# Revit family: МПА_В_Е_1000_4000_А31_Eng
name_source: partatom
category: Mechanical Equipment
units: mm (PartAtom-declared; Revit-internal decimal feet)

## family parameters
Always vertical = Yes
Classification = None
Cut with Voids When Loaded = No
Part Type = Normal
Room Calculation Point = No
Round Connector Dimension = Use Diameter
Shared = No
Work Plane-Based = No

## types (40) — shared parameters
00_20_Manufacturer = Vents
00_20_Name = Air supply unit
BW2 = 80 mm  [stored 0.262467 ft]
Casing Material = Steel, galvanized
Filter = Coarse 90%/G4
Frequency = 50 Hz
L5 = 400 mm  [stored 1.31234 ft]
Load Classification = HVAC
Maintenance zone material = <By Category>
Manufacturer = Vents
URL = https://ventilation-system.com
zero-valued in all types: Default Elevation

## per-type parameters (varying)
- MPA 1000 W ЕС L А31: 00_20_Type=MPA 1000 W ЕС L А31; Amperage=1 A; B=746 mm; B1=653 mm; B2=600 mm; B3=706 mm; B31=400 mm  [stored 1.31234 ft]; BE=753 mm; BW1=720 mm; E=400 mm  [stored 1.31234 ft]; H=393 mm  [stored 1.28937 ft]; H1=373 mm  [stored 1.22375 ft]; H3=200 mm  [stored 0.656168 ft]; HE=293 mm; HW1=62 mm; HW2=312 mm; Height=393 mm  [stored 1.28937 ft]; L=840 mm; L1=770 mm; L3=250 mm  [stored 0.82021 ft]; L6=100 mm  [stored 0.328084 ft]; LN=620 mm; Left=Yes; Length=900 mm; Maximum Air Flow=920.0 m³/h; Number of Fase=1; Panel side=Yes; Power=165 W; Right=No; Voltage=230 V; Water=Yes; Width=746 mm; d=25 mm  [stored 0.082021 ft]; l1=385 mm  [stored 1.26312 ft]
- MPA 4000 W ЕС L А31: 00_20_Type=MPA 4000 W ЕС L А31; Amperage=1 A; B=1087 mm; B1=993 mm; B2=940 mm; B3=1046 mm; B31=700 mm; BE=1093 mm; BW1=1060 mm; E=570 mm; H=563 mm; H1=543 mm  [stored 1.7815 ft]; H3=400 mm  [stored 1.31234 ft]; HE=463 mm  [stored 1.51903 ft]; HW1=82 mm; HW2=462 mm; Height=563 mm; L=1140 mm; L1=1070 mm; L3=380 mm  [stored 1.24672 ft]; L6=100 mm  [stored 0.328084 ft]; LN=770 mm; Left=Yes; Length=1200 mm; Maximum Air Flow=4950.0 m³/h; Number of Fase=1; Panel side=Yes; Power=698 W; Right=No; Voltage=230 V; Water=Yes; Width=1087 mm; d=35 mm  [stored 0.114829 ft]; l1=535 mm  [stored 1.75525 ft]
- MPA 1000 Е-6.0 ЕС L А31: 00_20_Type=MPA 1000 Е-6.0 ЕС L А31; Amperage=11 A; B=746 mm; B1=653 mm; B2=600 mm; B3=706 mm; B31=400 mm  [stored 1.31234 ft]; BE=753 mm; BW1=720 mm; E=400 mm  [stored 1.31234 ft]; H=393 mm  [stored 1.28937 ft]; H1=373 mm  [stored 1.22375 ft]; H3=200 mm  [stored 0.656168 ft]; HE=293 mm; HW1=62 mm; HW2=312 mm; Height=393 mm  [stored 1.28937 ft]; L=840 mm; L1=770 mm; L3=250 mm  [stored 0.82021 ft]; L6=220 mm  [stored 0.721785 ft]; LN=100 mm  [stored 0.328084 ft]; Left=Yes; Length=900 mm; Maximum Air Flow=1000.0 m³/h; Number of Fase=3; Panel side=Yes; Power=6165 W; Right=No; Voltage=400 V; Water=No; Width=746 mm; d=25 mm  [stored 0.082021 ft]; l1=385 mm  [stored 1.26312 ft]
- MPA 1500 W ЕС L А31: 00_20_Type=MPA 1500 W ЕС L А31; Amperage=2 A; B=847 mm; B1=754 mm; B2=700 mm; B3=808 mm; B31=500 mm  [stored 1.64042 ft]; BE=854 mm; BW1=820 mm; E=450 mm  [stored 1.47638 ft]; H=453 mm  [stored 1.48622 ft]; H1=433 mm; H3=250 mm  [stored 0.82021 ft]; HE=353 mm  [stored 1.15814 ft]; HW1=58 mm  [stored 0.190289 ft]; HW2=376 mm; Height=453 mm  [stored 1.48622 ft]; L=840 mm; L1=770 mm; L3=318 mm  [stored 1.04331 ft]; L6=100 mm  [stored 0.328084 ft]; LN=620 mm; Left=Yes; Length=900 mm; Maximum Air Flow=1145.0 m³/h; Number of Fase=1; Panel side=Yes; Power=222 W; Right=No; Voltage=230 V; Water=Yes; Width=847 mm; d=25 mm  [stored 0.082021 ft]; l1=385 mm  [stored 1.26312 ft]
- MPA 2000 W ЕС L А31: 00_20_Type=MPA 2000 W ЕС L А31; Amperage=2 A; B=847 mm; B1=754 mm; B2=700 mm; B3=808 mm; B31=500 mm  [stored 1.64042 ft]; BE=854 mm; BW1=820 mm; E=450 mm  [stored 1.47638 ft]; H=453 mm  [stored 1.48622 ft]; H1=433 mm; H3=300 mm; HE=353 mm  [stored 1.15814 ft]; HW1=58 mm  [stored 0.190289 ft]; HW2=376 mm; Height=453 mm  [stored 1.48622 ft]; L=840 mm; L1=770 mm; L3=318 mm  [stored 1.04331 ft]; L6=100 mm  [stored 0.328084 ft]; LN=620 mm; Left=Yes; Length=900 mm; Maximum Air Flow=2150.0 m³/h; Number of Fase=1; Panel side=Yes; Power=387 W; Right=No; Voltage=230 V; Water=Yes; Width=847 mm; d=25 mm  [stored 0.082021 ft]; l1=385 mm  [stored 1.26312 ft]
- MPA 3000 W ЕС L А31: 00_20_Type=MPA 3000 W ЕС L А31; Amperage=2 A; B=944 mm; B1=853 mm; B2=800 mm; B3=906 mm; B31=600 mm; BE=953 mm; BW1=920 mm; E=500 mm  [stored 1.64042 ft]; H=513 mm  [stored 1.68307 ft]; H1=493 mm  [stored 1.61745 ft]; H3=300 mm; HE=413 mm  [stored 1.35499 ft]; HW1=63 mm; HW2=431 mm; Height=513 mm  [stored 1.68307 ft]; L=1140 mm; L1=1070 mm; L3=368 mm  [stored 1.20735 ft]; L6=100 mm  [stored 0.328084 ft]; LN=770 mm; Left=Yes; Length=1200 mm; Maximum Air Flow=2930.0 m³/h; Number of Fase=1; Panel side=Yes; Power=425 W; Right=No; Voltage=230 V; Water=Yes; Width=944 mm; d=28 mm  [stored 0.0918635 ft]; l1=535 mm  [stored 1.75525 ft]
- MPA 1000 Е-12.0 ЕС L А31: 00_20_Type=MPA 1000 Е-12.0 ЕС L А31; Amperage=20 A; B=746 mm; B1=653 mm; B2=600 mm; B3=706 mm; B31=400 mm  [stored 1.31234 ft]; BE=753 mm; BW1=720 mm; E=400 mm  [stored 1.31234 ft]; H=393 mm  [stored 1.28937 ft]; H1=373 mm  [stored 1.22375 ft]; H3=200 mm  [stored 0.656168 ft]; HE=293 mm; HW1=62 mm; HW2=312 mm; Height=393 mm  [stored 1.28937 ft]; L=840 mm; L1=770 mm; L3=250 mm  [stored 0.82021 ft]; L6=220 mm  [stored 0.721785 ft]; LN=100 mm  [stored 0.328084 ft]; Left=Yes; Length=900 mm; Maximum Air Flow=1000.0 m³/h; Number of Fase=3; Panel side=Yes; Power=12165 W; Right=No; Voltage=400 V; Water=No; Width=746 mm; d=25 mm  [stored 0.082021 ft]; l1=385 mm  [stored 1.26312 ft]
- MPA 1000 Е-15.0 ЕС L А31: 00_20_Type=MPA 1000 Е-15.0 ЕС L А31; Amperage=24 A; B=746 mm; B1=653 mm; B2=600 mm; B3=706 mm; B31=400 mm  [stored 1.31234 ft]; BE=753 mm; BW1=720 mm; E=400 mm  [stored 1.31234 ft]; H=393 mm  [stored 1.28937 ft]; H1=373 mm  [stored 1.22375 ft]; H3=200 mm  [stored 0.656168 ft]; HE=293 mm; HW1=62 mm; HW2=312 mm; Height=393 mm  [stored 1.28937 ft]; L=840 mm; L1=770 mm; L3=250 mm  [stored 0.82021 ft]; L6=220 mm  [stored 0.721785 ft]; LN=100 mm  [stored 0.328084 ft]; Left=Yes; Length=900 mm; Maximum Air Flow=1000.0 m³/h; Number of Fase=3; Panel side=Yes; Power=15165 W; Right=No; Voltage=400 V; Water=No; Width=746 mm; d=25 mm  [stored 0.082021 ft]; l1=385 mm  [stored 1.26312 ft]
- MPA 1500 Е-9.0 ЕС L А31: 00_20_Type=MPA 1500 Е-9.0 ЕС L А31; Amperage=15 A; B=847 mm; B1=754 mm; B2=700 mm; B3=808 mm; B31=500 mm  [stored 1.64042 ft]; BE=854 mm; BW1=820 mm; E=450 mm  [stored 1.47638 ft]; H=453 mm  [stored 1.48622 ft]; H1=433 mm; H3=250 mm  [stored 0.82021 ft]; HE=353 mm  [stored 1.15814 ft]; HW1=58 mm  [stored 0.190289 ft]; HW2=376 mm; Height=453 mm  [stored 1.48622 ft]; L=840 mm; L1=770 mm; L3=318 mm  [stored 1.04331 ft]; L6=220 mm  [stored 0.721785 ft]; LN=100 mm  [stored 0.328084 ft]; Left=Yes; Length=900 mm; Maximum Air Flow=1500.0 m³/h; Number of Fase=3; Panel side=Yes; Power=9223 W; Right=No; Voltage=400 V; Water=No; Width=847 mm; d=25 mm  [stored 0.082021 ft]; l1=385 mm  [stored 1.26312 ft]
- MPA 1500 Е-14.0 ЕС L А31: 00_20_Type=MPA 1500 Е-14.0 ЕС L А31; Amperage=23 A; B=847 mm; B1=754 mm; B2=700 mm; B3=808 mm; B31=500 mm  [stored 1.64042 ft]; BE=854 mm; BW1=820 mm; E=450 mm  [stored 1.47638 ft]; H=453 mm  [stored 1.48622 ft]; H1=433 mm; H3=250 mm  [stored 0.82021 ft]; HE=353 mm  [stored 1.15814 ft]; HW1=58 mm  [stored 0.190289 ft]; HW2=376 mm; Height=453 mm  [stored 1.48622 ft]; L=840 mm; L1=770 mm; L3=318 mm  [stored 1.04331 ft]; L6=220 mm  [stored 0.721785 ft]; LN=100 mm  [stored 0.328084 ft]; Left=Yes; Length=900 mm; Maximum Air Flow=1500.0 m³/h; Number of Fase=3; Panel side=Yes; Power=14223 W; Right=No; Voltage=400 V; Water=No; Width=847 mm; d=25 mm  [stored 0.082021 ft]; l1=385 mm  [stored 1.26312 ft]
- MPA 1500 Е-18.0 ЕС L А31: 00_20_Type=MPA 1500 Е-18.0 ЕС L А31; Amperage=29 A; B=847 mm; B1=754 mm; B2=700 mm; B3=808 mm; B31=500 mm  [stored 1.64042 ft]; BE=854 mm; BW1=820 mm; E=450 mm  [stored 1.47638 ft]; H=453 mm  [stored 1.48622 ft]; H1=433 mm; H3=250 mm  [stored 0.82021 ft]; HE=353 mm  [stored 1.15814 ft]; HW1=58 mm  [stored 0.190289 ft]; HW2=376 mm; Height=453 mm  [stored 1.48622 ft]; L=840 mm; L1=770 mm; L3=318 mm  [stored 1.04331 ft]; L6=220 mm  [stored 0.721785 ft]; LN=100 mm  [stored 0.328084 ft]; Left=Yes; Length=900 mm; Maximum Air Flow=1500.0 m³/h; Number of Fase=3; Panel side=Yes; Power=18223 W; Right=No; Voltage=400 V; Water=No; Width=847 mm; d=25 mm  [stored 0.082021 ft]; l1=385 mm  [stored 1.26312 ft]
- MPA 2000 Е-12.0 ЕС L А31: 00_20_Type=MPA 2000 Е-12.0 ЕС L А31; Amperage=20 A; B=847 mm; B1=754 mm; B2=700 mm; B3=808 mm; B31=500 mm  [stored 1.64042 ft]; BE=854 mm; BW1=820 mm; E=450 mm  [stored 1.47638 ft]; H=453 mm  [stored 1.48622 ft]; H1=433 mm; H3=300 mm; HE=353 mm  [stored 1.15814 ft]; HW1=58 mm  [stored 0.190289 ft]; HW2=376 mm; Height=453 mm  [stored 1.48622 ft]; L=840 mm; L1=770 mm; L3=318 mm  [stored 1.04331 ft]; L6=220 mm  [stored 0.721785 ft]; LN=100 mm  [stored 0.328084 ft]; Left=Yes; Length=900 mm; Maximum Air Flow=2450.0 m³/h; Number of Fase=3; Panel side=Yes; Power=12406 W; Right=No; Voltage=400 V; Water=No; Width=847 mm; d=25 mm  [stored 0.082021 ft]; l1=385 mm  [stored 1.26312 ft]
- MPA 2000 Е-18.0 ЕС L А31: 00_20_Type=MPA 2000 Е-18.0 ЕС L А31; Amperage=30 A; B=847 mm; B1=754 mm; B2=700 mm; B3=808 mm; B31=500 mm  [stored 1.64042 ft]; BE=854 mm; BW1=820 mm; E=450 mm  [stored 1.47638 ft]; H=453 mm  [stored 1.48622 ft]; H1=433 mm; H3=300 mm; HE=353 mm  [stored 1.15814 ft]; HW1=58 mm  [stored 0.190289 ft]; HW2=376 mm; Height=453 mm  [stored 1.48622 ft]; L=840 mm; L1=770 mm; L3=318 mm  [stored 1.04331 ft]; L6=220 mm  [stored 0.721785 ft]; LN=100 mm  [stored 0.328084 ft]; Left=Yes; Length=900 mm; Maximum Air Flow=2450.0 m³/h; Number of Fase=3; Panel side=Yes; Power=18406 W; Right=No; Voltage=400 V; Water=No; Width=847 mm; d=25 mm  [stored 0.082021 ft]; l1=385 mm  [stored 1.26312 ft]
- MPA 2000 Е-24.0 ЕС L А31: 00_20_Type=MPA 2000 Е-24.0 ЕС L А31; Amperage=39 A; B=847 mm; B1=754 mm; B2=700 mm; B3=808 mm; B31=500 mm  [stored 1.64042 ft]; BE=854 mm; BW1=820 mm; E=450 mm  [stored 1.47638 ft]; H=453 mm  [stored 1.48622 ft]; H1=433 mm; H3=300 mm; HE=353 mm  [stored 1.15814 ft]; HW1=58 mm  [stored 0.190289 ft]; HW2=376 mm; Height=453 mm  [stored 1.48622 ft]; L=840 mm; L1=770 mm; L3=318 mm  [stored 1.04331 ft]; L6=220 mm  [stored 0.721785 ft]; LN=100 mm  [stored 0.328084 ft]; Left=Yes; Length=900 mm; Maximum Air Flow=2450.0 m³/h; Number of Fase=3; Panel side=Yes; Power=24406 W; Right=No; Voltage=400 V; Water=No; Width=847 mm; d=25 mm  [stored 0.082021 ft]; l1=385 mm  [stored 1.26312 ft]
- MPA 3000 Е-18.0 ЕС L А31: 00_20_Type=MPA 3000 Е-18.0 ЕС L А31; Amperage=30 A; B=944 mm; B1=853 mm; B2=800 mm; B3=906 mm; B31=600 mm; BE=953 mm; BW1=920 mm; E=500 mm  [stored 1.64042 ft]; H=513 mm  [stored 1.68307 ft]; H1=493 mm  [stored 1.61745 ft]; H3=300 mm; HE=413 mm  [stored 1.35499 ft]; HW1=63 mm; HW2=431 mm; Height=513 mm  [stored 1.68307 ft]; L=1140 mm; L1=1070 mm; L3=368 mm  [stored 1.20735 ft]; L6=370 mm  [stored 1.21391 ft]; LN=100 mm  [stored 0.328084 ft]; Left=Yes; Length=1200 mm; Maximum Air Flow=3150.0 m³/h; Number of Fase=3; Panel side=Yes; Power=18472 W; Right=No; Voltage=400 V; Water=No; Width=944 mm; d=28 mm  [stored 0.0918635 ft]; l1=535 mm  [stored 1.75525 ft]
- MPA 3000 Е-27.0 ЕС L А31: 00_20_Type=MPA 3000 Е-27.0 ЕС L А31; Amperage=44 A; B=944 mm; B1=853 mm; B2=800 mm; B3=906 mm; B31=600 mm; BE=953 mm; BW1=920 mm; E=500 mm  [stored 1.64042 ft]; H=513 mm  [stored 1.68307 ft]; H1=493 mm  [stored 1.61745 ft]; H3=300 mm; HE=413 mm  [stored 1.35499 ft]; HW1=63 mm; HW2=431 mm; Height=513 mm  [stored 1.68307 ft]; L=1140 mm; L1=1070 mm; L3=368 mm  [stored 1.20735 ft]; L6=370 mm  [stored 1.21391 ft]; LN=100 mm  [stored 0.328084 ft]; Left=Yes; Length=1200 mm; Maximum Air Flow=3150.0 m³/h; Number of Fase=3; Panel side=Yes; Power=27472 W; Right=No; Voltage=400 V; Water=No; Width=944 mm; d=28 mm  [stored 0.0918635 ft]; l1=535 mm  [stored 1.75525 ft]
- MPA 3000 Е-45.0 ЕС L А31: 00_20_Type=MPA 3000 Е-45.0 ЕС L А31; Amperage=73 A; B=944 mm; B1=853 mm; B2=800 mm; B3=906 mm; B31=600 mm; BE=953 mm; BW1=920 mm; E=500 mm  [stored 1.64042 ft]; H=513 mm  [stored 1.68307 ft]; H1=493 mm  [stored 1.61745 ft]; H3=300 mm; HE=413 mm  [stored 1.35499 ft]; HW1=63 mm; HW2=431 mm; Height=513 mm  [stored 1.68307 ft]; L=1140 mm; L1=1070 mm; L3=368 mm  [stored 1.20735 ft]; L6=370 mm  [stored 1.21391 ft]; LN=100 mm  [stored 0.328084 ft]; Left=Yes; Length=1200 mm; Maximum Air Flow=3150.0 m³/h; Number of Fase=3; Panel side=Yes; Power=45472 W; Right=No; Voltage=400 V; Water=No; Width=944 mm; d=28 mm  [stored 0.0918635 ft]; l1=535 mm  [stored 1.75525 ft]
- MPA 4000 Е-45.0 ЕС L А31: 00_20_Type=MPA 4000 Е-45.0 ЕС L А31; Amperage=73 A; B=1087 mm; B1=993 mm; B2=940 mm; B3=1046 mm; B31=700 mm; BE=1093 mm; BW1=1060 mm; E=570 mm; H=563 mm; H1=543 mm  [stored 1.7815 ft]; H3=400 mm  [stored 1.31234 ft]; HE=463 mm  [stored 1.51903 ft]; HW1=82 mm; HW2=462 mm; Height=563 mm; L=1140 mm; L1=1070 mm; L3=380 mm  [stored 1.24672 ft]; L6=370 mm  [stored 1.21391 ft]; LN=100 mm  [stored 0.328084 ft]; Left=Yes; Length=1200 mm; Maximum Air Flow=5000.0 m³/h; Number of Fase=3; Panel side=Yes; Power=45717 W; Right=No; Voltage=400 V; Water=No; Width=1087 mm; d=35 mm  [stored 0.114829 ft]; l1=535 mm  [stored 1.75525 ft]
- MPA 4000 Е-24.0 ЕС L А31: 00_20_Type=MPA 4000 Е-24.0 ЕС L А31; Amperage=43 A; B=1087 mm; B1=993 mm; B2=940 mm; B3=1046 mm; B31=700 mm; BE=1093 mm; BW1=1060 mm; E=570 mm; H=563 mm; H1=543 mm  [stored 1.7815 ft]; H3=400 mm  [stored 1.31234 ft]; HE=463 mm  [stored 1.51903 ft]; HW1=82 mm; HW2=462 mm; Height=563 mm; L=1140 mm; L1=1070 mm; L3=380 mm  [stored 1.24672 ft]; L6=370 mm  [stored 1.21391 ft]; LN=100 mm  [stored 0.328084 ft]; Left=Yes; Length=1200 mm; Maximum Air Flow=5000.0 m³/h; Number of Fase=3; Panel side=Yes; Power=24717 W; Right=No; Voltage=400 V; Water=No; Width=1087 mm; d=35 mm  [stored 0.114829 ft]; l1=535 mm  [stored 1.75525 ft]
- MPA 4000 Е-54.0 ЕС L А31: 00_20_Type=MPA 4000 Е-54.0 ЕС L А31; Amperage=88 A; B=1087 mm; B1=993 mm; B2=940 mm; B3=1046 mm; B31=700 mm; BE=1093 mm; BW1=1060 mm; E=570 mm; H=563 mm; H1=543 mm  [stored 1.7815 ft]; H3=400 mm  [stored 1.31234 ft]; HE=463 mm  [stored 1.51903 ft]; HW1=82 mm; HW2=462 mm; Height=563 mm; L=1140 mm; L1=1070 mm; L3=380 mm  [stored 1.24672 ft]; L6=370 mm  [stored 1.21391 ft]; LN=100 mm  [stored 0.328084 ft]; Left=Yes; Length=1200 mm; Maximum Air Flow=5000.0 m³/h; Number of Fase=3; Panel side=Yes; Power=54717 W; Right=No; Voltage=400 V; Water=No; Width=1087 mm; d=35 mm  [stored 0.114829 ft]; l1=535 mm  [stored 1.75525 ft]
- MPA 1000 W ЕС R А31: 00_20_Type=MPA 1000 W ЕС R А31; Amperage=1 A; B=746 mm; B1=653 mm; B2=600 mm; B3=706 mm; B31=400 mm  [stored 1.31234 ft]; BE=47 mm  [stored 0.154199 ft]; BW1=720 mm; E=400 mm  [stored 1.31234 ft]; H=393 mm  [stored 1.28937 ft]; H1=373 mm  [stored 1.22375 ft]; H3=200 mm  [stored 0.656168 ft]; HE=293 mm; HW1=62 mm; HW2=312 mm; Height=393 mm  [stored 1.28937 ft]; L=840 mm; L1=770 mm; L3=250 mm  [stored 0.82021 ft]; L6=100 mm  [stored 0.328084 ft]; LN=620 mm; Left=No; Length=900 mm; Maximum Air Flow=920.0 m³/h; Number of Fase=1; Panel side=Yes; Power=165 W; Right=Yes; Voltage=230 V; Water=Yes; Width=746 mm; d=25 mm  [stored 0.082021 ft]; l1=385 mm  [stored 1.26312 ft]
- MPA 1000 Е-12.0 ЕС R А31: 00_20_Type=MPA 1000 Е-12.0 ЕС R А31; Amperage=20 A; B=746 mm; B1=653 mm; B2=600 mm; B3=706 mm; B31=400 mm  [stored 1.31234 ft]; BE=47 mm  [stored 0.154199 ft]; BW1=720 mm; E=400 mm  [stored 1.31234 ft]; H=393 mm  [stored 1.28937 ft]; H1=373 mm  [stored 1.22375 ft]; H3=200 mm  [stored 0.656168 ft]; HE=293 mm; HW1=62 mm; HW2=312 mm; Height=393 mm  [stored 1.28937 ft]; L=840 mm; L1=770 mm; L3=250 mm  [stored 0.82021 ft]; L6=220 mm  [stored 0.721785 ft]; LN=100 mm  [stored 0.328084 ft]; Left=No; Length=900 mm; Maximum Air Flow=1000.0 m³/h; Number of Fase=3; Panel side=Yes; Power=12165 W; Right=Yes; Voltage=400 V; Water=No; Width=746 mm; d=25 mm  [stored 0.082021 ft]; l1=385 mm  [stored 1.26312 ft]
- MPA 1000 Е-15.0 ЕС R А31: 00_20_Type=MPA 1000 Е-15.0 ЕС R А31; Amperage=24 A; B=746 mm; B1=653 mm; B2=600 mm; B3=706 mm; B31=400 mm  [stored 1.31234 ft]; BE=47 mm  [stored 0.154199 ft]; BW1=720 mm; E=400 mm  [stored 1.31234 ft]; H=393 mm  [stored 1.28937 ft]; H1=373 mm  [stored 1.22375 ft]; H3=200 mm  [stored 0.656168 ft]; HE=293 mm; HW1=62 mm; HW2=312 mm; Height=393 mm  [stored 1.28937 ft]; L=840 mm; L1=770 mm; L3=250 mm  [stored 0.82021 ft]; L6=220 mm  [stored 0.721785 ft]; LN=100 mm  [stored 0.328084 ft]; Left=No; Length=900 mm; Maximum Air Flow=1000.0 m³/h; Number of Fase=3; Panel side=Yes; Power=15165 W; Right=Yes; Voltage=400 V; Water=No; Width=746 mm; d=25 mm  [stored 0.082021 ft]; l1=385 mm  [stored 1.26312 ft]
- MPA 1000 Е-6.0 ЕС R А31: 00_20_Type=MPA 1000 Е-6.0 ЕС R А31; Amperage=11 A; B=746 mm; B1=653 mm; B2=600 mm; B3=706 mm; B31=400 mm  [stored 1.31234 ft]; BE=47 mm  [stored 0.154199 ft]; BW1=720 mm; E=400 mm  [stored 1.31234 ft]; H=393 mm  [stored 1.28937 ft]; H1=373 mm  [stored 1.22375 ft]; H3=200 mm  [stored 0.656168 ft]; HE=293 mm; HW1=62 mm; HW2=312 mm; Height=393 mm  [stored 1.28937 ft]; L=840 mm; L1=770 mm; L3=250 mm  [stored 0.82021 ft]; L6=220 mm  [stored 0.721785 ft]; LN=100 mm  [stored 0.328084 ft]; Left=No; Length=900 mm; Maximum Air Flow=1000.0 m³/h; Number of Fase=3; Panel side=Yes; Power=6165 W; Right=Yes; Voltage=400 V; Water=No; Width=746 mm; d=25 mm  [stored 0.082021 ft]; l1=385 mm  [stored 1.26312 ft]
- MPA 1500 W ЕС R А31: 00_20_Type=MPA 1500 W ЕС L А31; Amperage=2 A; B=847 mm; B1=754 mm; B2=700 mm; B3=808 mm; B31=500 mm  [stored 1.64042 ft]; BE=46 mm  [stored 0.150919 ft]; BW1=820 mm; E=450 mm  [stored 1.47638 ft]; H=453 mm  [stored 1.48622 ft]; H1=433 mm; H3=250 mm  [stored 0.82021 ft]; HE=353 mm  [stored 1.15814 ft]; HW1=58 mm  [stored 0.190289 ft]; HW2=376 mm; Height=453 mm  [stored 1.48622 ft]; L=840 mm; L1=770 mm; L3=318 mm  [stored 1.04331 ft]; L6=100 mm  [stored 0.328084 ft]; LN=620 mm; Left=No; Length=900 mm; Maximum Air Flow=1145.0 m³/h; Number of Fase=1; Panel side=Yes; Power=222 W; Right=Yes; Voltage=230 V; Water=Yes; Width=847 mm; d=25 mm  [stored 0.082021 ft]; l1=385 mm  [stored 1.26312 ft]
- MPA 1500 Е-14.0 ЕС R А31: 00_20_Type=MPA 1500 Е-14.0 ЕС R А31; Amperage=23 A; B=847 mm; B1=754 mm; B2=700 mm; B3=808 mm; B31=500 mm  [stored 1.64042 ft]; BE=46 mm  [stored 0.150919 ft]; BW1=820 mm; E=450 mm  [stored 1.47638 ft]; H=453 mm  [stored 1.48622 ft]; H1=433 mm; H3=250 mm  [stored 0.82021 ft]; HE=353 mm  [stored 1.15814 ft]; HW1=58 mm  [stored 0.190289 ft]; HW2=376 mm; Height=453 mm  [stored 1.48622 ft]; L=840 mm; L1=770 mm; L3=318 mm  [stored 1.04331 ft]; L6=220 mm  [stored 0.721785 ft]; LN=100 mm  [stored 0.328084 ft]; Left=No; Length=900 mm; Maximum Air Flow=1500.0 m³/h; Number of Fase=3; Panel side=Yes; Power=14223 W; Right=Yes; Voltage=400 V; Water=No; Width=847 mm; d=25 mm  [stored 0.082021 ft]; l1=385 mm  [stored 1.26312 ft]
- MPA 1500 Е-18.0 ЕС R А31: 00_20_Type=MPA 1500 Е-18.0 ЕС R А31; Amperage=29 A; B=847 mm; B1=754 mm; B2=700 mm; B3=808 mm; B31=500 mm  [stored 1.64042 ft]; BE=46 mm  [stored 0.150919 ft]; BW1=820 mm; E=450 mm  [stored 1.47638 ft]; H=453 mm  [stored 1.48622 ft]; H1=433 mm; H3=250 mm  [stored 0.82021 ft]; HE=353 mm  [stored 1.15814 ft]; HW1=58 mm  [stored 0.190289 ft]; HW2=376 mm; Height=453 mm  [stored 1.48622 ft]; L=840 mm; L1=770 mm; L3=318 mm  [stored 1.04331 ft]; L6=220 mm  [stored 0.721785 ft]; LN=100 mm  [stored 0.328084 ft]; Left=No; Length=900 mm; Maximum Air Flow=1500.0 m³/h; Number of Fase=3; Panel side=Yes; Power=18223 W; Right=Yes; Voltage=400 V; Water=No; Width=847 mm; d=25 mm  [stored 0.082021 ft]; l1=385 mm  [stored 1.26312 ft]
- MPA 1500 Е-9.0 ЕС R А31: 00_20_Type=MPA 1500 Е-9.0 ЕС R А31; Amperage=15 A; B=847 mm; B1=754 mm; B2=700 mm; B3=808 mm; B31=500 mm  [stored 1.64042 ft]; BE=46 mm  [stored 0.150919 ft]; BW1=820 mm; E=450 mm  [stored 1.47638 ft]; H=453 mm  [stored 1.48622 ft]; H1=433 mm; H3=250 mm  [stored 0.82021 ft]; HE=353 mm  [stored 1.15814 ft]; HW1=58 mm  [stored 0.190289 ft]; HW2=376 mm; Height=453 mm  [stored 1.48622 ft]; L=840 mm; L1=770 mm; L3=318 mm  [stored 1.04331 ft]; L6=220 mm  [stored 0.721785 ft]; LN=100 mm  [stored 0.328084 ft]; Left=No; Length=900 mm; Maximum Air Flow=1500.0 m³/h; Number of Fase=3; Panel side=Yes; Power=9223 W; Right=Yes; Voltage=400 V; Water=No; Width=847 mm; d=25 mm  [stored 0.082021 ft]; l1=385 mm  [stored 1.26312 ft]
- MPA 2000 W ЕС R А31: 00_20_Type=MPA 2000 W ЕС R А31; Amperage=2 A; B=847 mm; B1=754 mm; B2=700 mm; B3=808 mm; B31=500 mm  [stored 1.64042 ft]; BE=46 mm  [stored 0.150919 ft]; BW1=820 mm; E=450 mm  [stored 1.47638 ft]; H=453 mm  [stored 1.48622 ft]; H1=433 mm; H3=300 mm; HE=353 mm  [stored 1.15814 ft]; HW1=58 mm  [stored 0.190289 ft]; HW2=376 mm; Height=453 mm  [stored 1.48622 ft]; L=840 mm; L1=770 mm; L3=318 mm  [stored 1.04331 ft]; L6=100 mm  [stored 0.328084 ft]; LN=620 mm; Left=No; Length=900 mm; Maximum Air Flow=2150.0 m³/h; Number of Fase=1; Panel side=Yes; Power=387 W; Right=Yes; Voltage=230 V; Water=Yes; Width=847 mm; d=25 mm  [stored 0.082021 ft]; l1=385 mm  [stored 1.26312 ft]
- MPA 2000 Е-12.0 ЕС R А31: 00_20_Type=MPA 2000 Е-12.0 ЕС R А31; Amperage=20 A; B=847 mm; B1=754 mm; B2=700 mm; B3=808 mm; B31=500 mm  [stored 1.64042 ft]; BE=46 mm  [stored 0.150919 ft]; BW1=820 mm; E=450 mm  [stored 1.47638 ft]; H=453 mm  [stored 1.48622 ft]; H1=433 mm; H3=300 mm; HE=353 mm  [stored 1.15814 ft]; HW1=58 mm  [stored 0.190289 ft]; HW2=376 mm; Height=453 mm  [stored 1.48622 ft]; L=840 mm; L1=770 mm; L3=318 mm  [stored 1.04331 ft]; L6=220 mm  [stored 0.721785 ft]; LN=100 mm  [stored 0.328084 ft]; Left=No; Length=900 mm; Maximum Air Flow=2450.0 m³/h; Number of Fase=3; Panel side=Yes; Power=12406 W; Right=Yes; Voltage=400 V; Water=No; Width=847 mm; d=25 mm  [stored 0.082021 ft]; l1=385 mm  [stored 1.26312 ft]
- MPA 2000 Е-18.0 ЕС R А31: 00_20_Type=MPA 2000 Е-18.0 ЕС R А31; Amperage=30 A; B=847 mm; B1=754 mm; B2=700 mm; B3=808 mm; B31=500 mm  [stored 1.64042 ft]; BE=46 mm  [stored 0.150919 ft]; BW1=820 mm; E=450 mm  [stored 1.47638 ft]; H=453 mm  [stored 1.48622 ft]; H1=433 mm; H3=300 mm; HE=353 mm  [stored 1.15814 ft]; HW1=58 mm  [stored 0.190289 ft]; HW2=376 mm; Height=453 mm  [stored 1.48622 ft]; L=840 mm; L1=770 mm; L3=318 mm  [stored 1.04331 ft]; L6=220 mm  [stored 0.721785 ft]; LN=100 mm  [stored 0.328084 ft]; Left=No; Length=900 mm; Maximum Air Flow=2450.0 m³/h; Number of Fase=3; Panel side=Yes; Power=18406 W; Right=Yes; Voltage=400 V; Water=No; Width=847 mm; d=25 mm  [stored 0.082021 ft]; l1=385 mm  [stored 1.26312 ft]
- MPA 2000 Е-24.0 ЕС R А31: 00_20_Type=MPA 2000 Е-24.0 ЕС R А31; Amperage=39 A; B=847 mm; B1=754 mm; B2=700 mm; B3=808 mm; B31=500 mm  [stored 1.64042 ft]; BE=46 mm  [stored 0.150919 ft]; BW1=820 mm; E=450 mm  [stored 1.47638 ft]; H=453 mm  [stored 1.48622 ft]; H1=433 mm; H3=300 mm; HE=353 mm  [stored 1.15814 ft]; HW1=58 mm  [stored 0.190289 ft]; HW2=376 mm; Height=453 mm  [stored 1.48622 ft]; L=840 mm; L1=770 mm; L3=318 mm  [stored 1.04331 ft]; L6=220 mm  [stored 0.721785 ft]; LN=100 mm  [stored 0.328084 ft]; Left=No; Length=900 mm; Maximum Air Flow=2450.0 m³/h; Number of Fase=3; Panel side=Yes; Power=24406 W; Right=Yes; Voltage=400 V; Water=No; Width=847 mm; d=25 mm  [stored 0.082021 ft]; l1=385 mm  [stored 1.26312 ft]
- MPA 3000 W ЕС R А31: 00_20_Type=MPA 3000 W ЕС R А31; Amperage=2 A; B=944 mm; B1=853 mm; B2=800 mm; B3=906 mm; B31=600 mm; BE=47 mm  [stored 0.154199 ft]; BW1=920 mm; E=500 mm  [stored 1.64042 ft]; H=513 mm  [stored 1.68307 ft]; H1=493 mm  [stored 1.61745 ft]; H3=300 mm; HE=413 mm  [stored 1.35499 ft]; HW1=63 mm; HW2=431 mm; Height=513 mm  [stored 1.68307 ft]; L=1140 mm; L1=1070 mm; L3=368 mm  [stored 1.20735 ft]; L6=100 mm  [stored 0.328084 ft]; LN=770 mm; Left=No; Length=1140 mm; Maximum Air Flow=2930.0 m³/h; Number of Fase=1; Panel side=No; Power=425 W; Right=Yes; Voltage=230 V; Water=Yes; Width=944 mm; d=28 mm  [stored 0.0918635 ft]; l1=535 mm  [stored 1.75525 ft]
- MPA 3000 Е-18.0 ЕС R А31: 00_20_Type=MPA 3000 Е-18.0 ЕС R А31; Amperage=30 A; B=944 mm; B1=853 mm; B2=800 mm; B3=906 mm; B31=600 mm; BE=47 mm  [stored 0.154199 ft]; BW1=920 mm; E=500 mm  [stored 1.64042 ft]; H=513 mm  [stored 1.68307 ft]; H1=493 mm  [stored 1.61745 ft]; H3=300 mm; HE=413 mm  [stored 1.35499 ft]; HW1=63 mm; HW2=431 mm; Height=513 mm  [stored 1.68307 ft]; L=1140 mm; L1=1070 mm; L3=368 mm  [stored 1.20735 ft]; L6=370 mm  [stored 1.21391 ft]; LN=100 mm  [stored 0.328084 ft]; Left=No; Length=1200 mm; Maximum Air Flow=3150.0 m³/h; Number of Fase=3; Panel side=Yes; Power=18472 W; Right=Yes; Voltage=400 V; Water=No; Width=944 mm; d=28 mm  [stored 0.0918635 ft]; l1=535 mm  [stored 1.75525 ft]
- MPA 3000 Е-27.0 ЕС R А31: 00_20_Type=MPA 3000 Е-27.0 ЕС R А31; Amperage=44 A; B=944 mm; B1=853 mm; B2=800 mm; B3=906 mm; B31=600 mm; BE=47 mm  [stored 0.154199 ft]; BW1=920 mm; E=500 mm  [stored 1.64042 ft]; H=513 mm  [stored 1.68307 ft]; H1=493 mm  [stored 1.61745 ft]; H3=300 mm; HE=413 mm  [stored 1.35499 ft]; HW1=63 mm; HW2=431 mm; Height=513 mm  [stored 1.68307 ft]; L=1140 mm; L1=1070 mm; L3=368 mm  [stored 1.20735 ft]; L6=370 mm  [stored 1.21391 ft]; LN=100 mm  [stored 0.328084 ft]; Left=No; Length=1200 mm; Maximum Air Flow=3150.0 m³/h; Number of Fase=3; Panel side=Yes; Power=27472 W; Right=Yes; Voltage=400 V; Water=No; Width=944 mm; d=28 mm  [stored 0.0918635 ft]; l1=535 mm  [stored 1.75525 ft]
- MPA 3000 Е-45.0 ЕС R А31: 00_20_Type=MPA 3000 Е-45.0 ЕС R А31; Amperage=73 A; B=944 mm; B1=853 mm; B2=800 mm; B3=906 mm; B31=600 mm; BE=47 mm  [stored 0.154199 ft]; BW1=920 mm; E=500 mm  [stored 1.64042 ft]; H=513 mm  [stored 1.68307 ft]; H1=493 mm  [stored 1.61745 ft]; H3=300 mm; HE=413 mm  [stored 1.35499 ft]; HW1=63 mm; HW2=431 mm; Height=513 mm  [stored 1.68307 ft]; L=1140 mm; L1=1070 mm; L3=368 mm  [stored 1.20735 ft]; L6=370 mm  [stored 1.21391 ft]; LN=100 mm  [stored 0.328084 ft]; Left=No; Length=1200 mm; Maximum Air Flow=3150.0 m³/h; Number of Fase=3; Panel side=Yes; Power=45472 W; Right=Yes; Voltage=400 V; Water=No; Width=944 mm; d=28 mm  [stored 0.0918635 ft]; l1=535 mm  [stored 1.75525 ft]
- MPA 4000 W ЕС R А31: 00_20_Type=MPA 4000 W ЕС R А31; Amperage=1 A; B=1087 mm; B1=993 mm; B2=940 mm; B3=1046 mm; B31=700 mm; BE=47 mm  [stored 0.154199 ft]; BW1=1060 mm; E=570 mm; H=563 mm; H1=543 mm  [stored 1.7815 ft]; H3=400 mm  [stored 1.31234 ft]; HE=463 mm  [stored 1.51903 ft]; HW1=82 mm; HW2=462 mm; Height=563 mm; L=1140 mm; L1=1070 mm; L3=380 mm  [stored 1.24672 ft]; L6=100 mm  [stored 0.328084 ft]; LN=770 mm; Left=No; Length=1200 mm; Maximum Air Flow=4950.0 m³/h; Number of Fase=1; Panel side=Yes; Power=698 W; Right=Yes; Voltage=230 V; Water=Yes; Width=1087 mm; d=35 mm  [stored 0.114829 ft]; l1=535 mm  [stored 1.75525 ft]
- MPA 4000 Е-24.0 ЕС R А31: 00_20_Type=MPA 4000 Е-24.0 ЕС R А31; Amperage=43 A; B=1087 mm; B1=993 mm; B2=940 mm; B3=1046 mm; B31=700 mm; BE=47 mm  [stored 0.154199 ft]; BW1=1060 mm; E=570 mm; H=563 mm; H1=543 mm  [stored 1.7815 ft]; H3=400 mm  [stored 1.31234 ft]; HE=463 mm  [stored 1.51903 ft]; HW1=82 mm; HW2=462 mm; Height=563 mm; L=1140 mm; L1=1070 mm; L3=380 mm  [stored 1.24672 ft]; L6=370 mm  [stored 1.21391 ft]; LN=100 mm  [stored 0.328084 ft]; Left=No; Length=1200 mm; Maximum Air Flow=5000.0 m³/h; Number of Fase=3; Panel side=Yes; Power=24717 W; Right=Yes; Voltage=400 V; Water=No; Width=1087 mm; d=35 mm  [stored 0.114829 ft]; l1=535 mm  [stored 1.75525 ft]
- MPA 4000 Е-45.0 ЕС R А31: 00_20_Type=MPA 4000 Е-45.0 ЕС R А31; Amperage=73 A; B=1087 mm; B1=993 mm; B2=940 mm; B3=1046 mm; B31=700 mm; BE=47 mm  [stored 0.154199 ft]; BW1=1060 mm; E=570 mm; H=563 mm; H1=543 mm  [stored 1.7815 ft]; H3=400 mm  [stored 1.31234 ft]; HE=463 mm  [stored 1.51903 ft]; HW1=82 mm; HW2=462 mm; Height=563 mm; L=1140 mm; L1=1070 mm; L3=380 mm  [stored 1.24672 ft]; L6=370 mm  [stored 1.21391 ft]; LN=100 mm  [stored 0.328084 ft]; Left=No; Length=1200 mm; Maximum Air Flow=5000.0 m³/h; Number of Fase=3; Panel side=Yes; Power=45717 W; Right=Yes; Voltage=400 V; Water=No; Width=1087 mm; d=35 mm  [stored 0.114829 ft]; l1=535 mm  [stored 1.75525 ft]
- MPA 4000 Е-54.0 ЕС R А31: 00_20_Type=MPA 4000 Е-54.0 ЕС R А31; Amperage=88 A; B=1087 mm; B1=993 mm; B2=940 mm; B3=1046 mm; B31=700 mm; BE=47 mm  [stored 0.154199 ft]; BW1=1060 mm; E=570 mm; H=563 mm; H1=543 mm  [stored 1.7815 ft]; H3=400 mm  [stored 1.31234 ft]; HE=463 mm  [stored 1.51903 ft]; HW1=82 mm; HW2=462 mm; Height=563 mm; L=1140 mm; L1=1070 mm; L3=380 mm  [stored 1.24672 ft]; L6=370 mm  [stored 1.21391 ft]; LN=100 mm  [stored 0.328084 ft]; Left=No; Length=1200 mm; Maximum Air Flow=5000.0 m³/h; Number of Fase=3; Panel side=Yes; Power=54717 W; Right=Yes; Voltage=400 V; Water=No; Width=1087 mm; d=35 mm  [stored 0.114829 ft]; l1=535 mm  [stored 1.75525 ft]

note: [stored X ft] marks values corroborated as IEEE doubles in the binary element streams (Revit-internal decimal feet)
